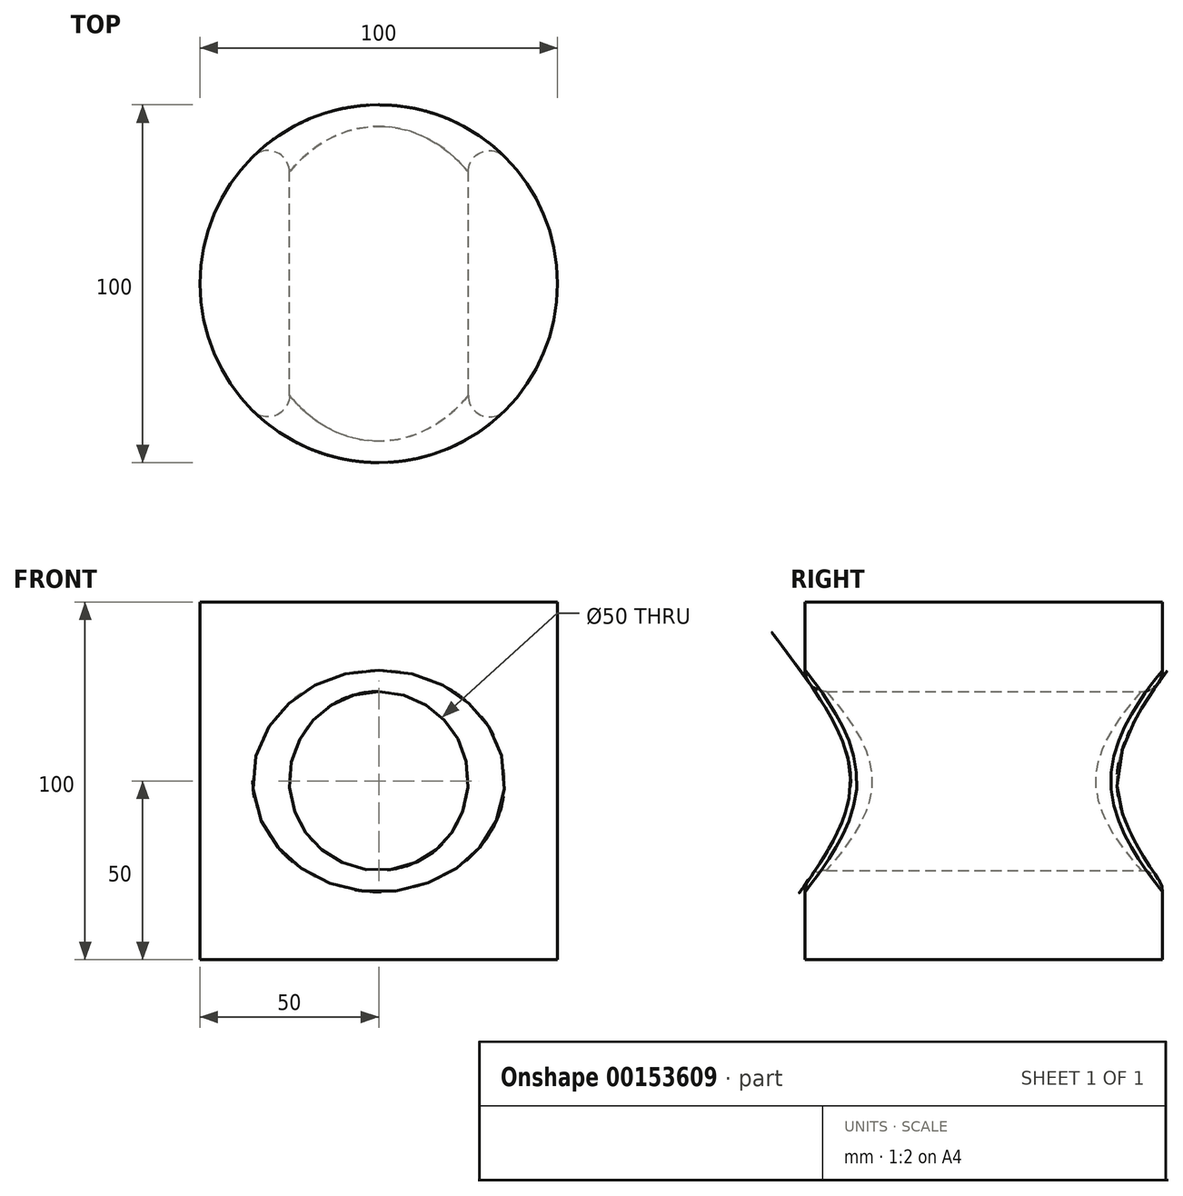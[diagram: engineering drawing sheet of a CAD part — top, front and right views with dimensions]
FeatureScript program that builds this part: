
annotation { "Feature Type Name" : "Feature", "Feature Type Description" : "" }
export const myFeature = defineFeature(function(context is Context, id is Id, definition is map)
    precondition{}
    {
        {
            var Q0;
            Q0=qCreatedBy(makeId("Top.planeOp"),FACE);
            var sketch = newSketch(context, id + "F0", { "sketchPlane" : qUnion([Q0])});
            skCircle(sketch, "E0", {"center": v(0, 0) * mm, "radius": 50 * mm});
            skSolve(sketch);
        }
        {
            var Q0;
            Q0 = qSketchRegion(id + "F0", true);
            extrude(context, id + "F1", {"entities" : qUnion([Q0]), "depth" : 100 * mm});
        }
        {
            var Q0;
            Q0=qCreatedBy(makeId("Front.planeOp"),FACE);
            var sketch = newSketch(context, id + "F2", { "sketchPlane" : qUnion([Q0])});
            skLineSegment(sketch, "E1", {"start": v(0, 100) * mm, "end": v(0, 0) * mm, "construction": true});
            skCircle(sketch, "E2", {"center": v(0, 50) * mm, "radius": 25 * mm});
            skSolve(sketch);
        }
        {
            var Q0;
            Q0 = qSketchRegion(id + "F2", true);
            extrude(context, id + "F3", {"entities" : qUnion([Q0]), "operationType" : NewBodyOperationType.REMOVE, "endBound" : BoundingType.SYMMETRIC, "depth" : 200 * mm});
        }
        {
            var Q0;
            Q0=makeQuery(id+"F3.boolean.opBoolean","COPY",FACE,{"derivedFrom":makeQuery(id+"F3.opExtrude","SWEPT_FACE",FACE,{"disambiguationData":[OSD([sQuery(id+"F2.wireOp",EDGE,"E2")])]})});
            fillet(context, id + "F4", {"entities" : qUnion([Q0]), "radius" : 6 * mm, "tangentPropagation" : true, "allowEdgeOverflow" : false});
        }
    });
